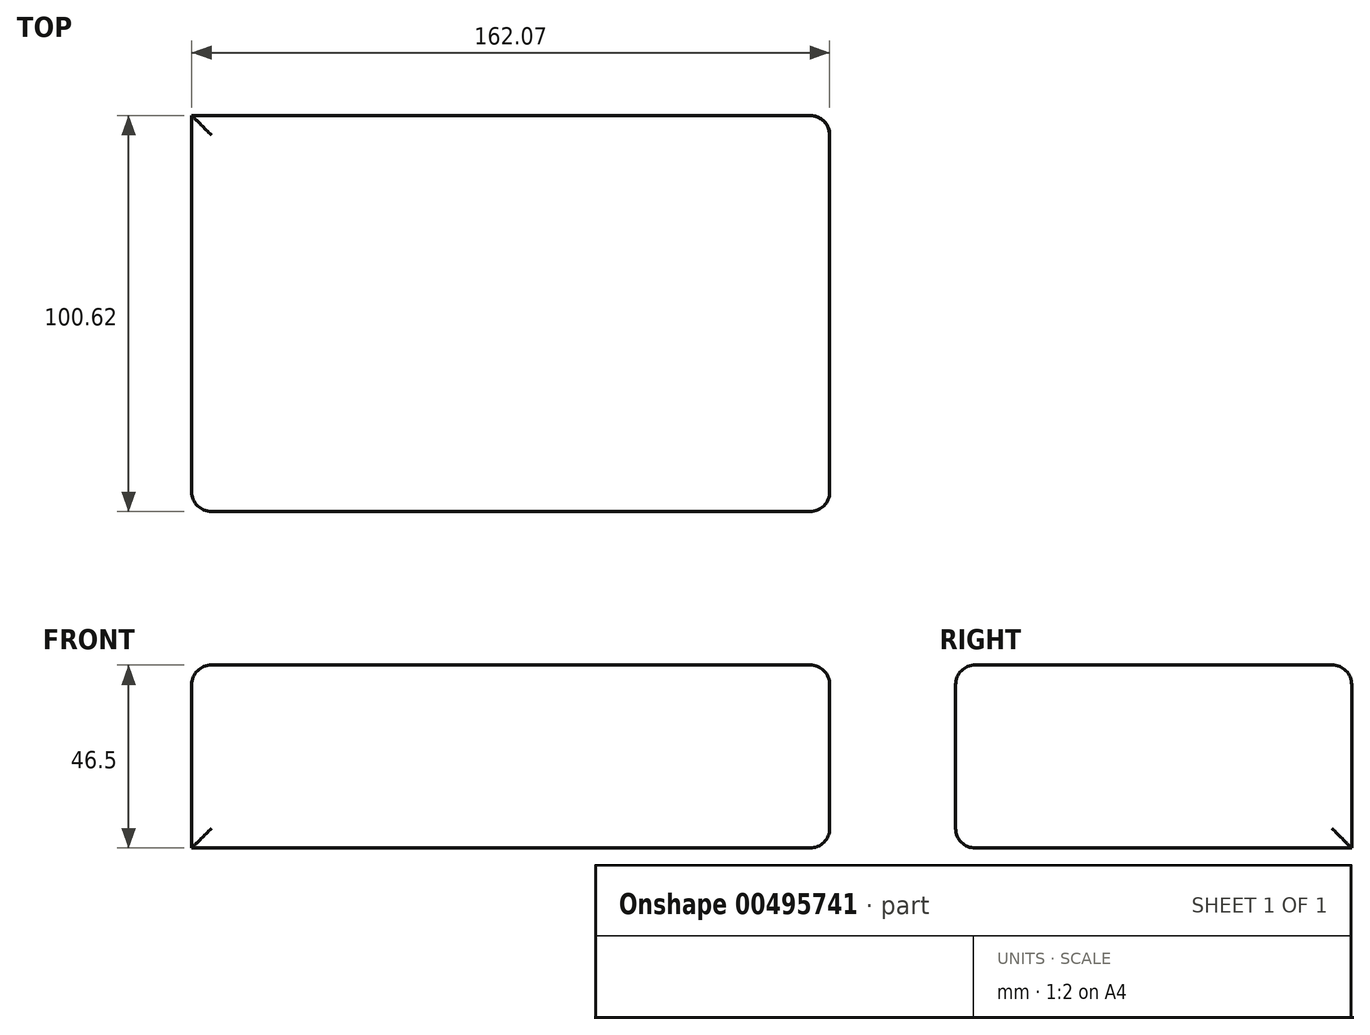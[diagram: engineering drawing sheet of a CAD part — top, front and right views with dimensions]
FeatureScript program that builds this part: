
annotation { "Feature Type Name" : "Feature", "Feature Type Description" : "" }
export const myFeature = defineFeature(function(context is Context, id is Id, definition is map)
    precondition{}
    {
        {
            var Q0;
            Q0=qCreatedBy(makeId("Top.planeOp"),FACE);
            var sketch = newSketch(context, id + "F0", { "sketchPlane" : qUnion([Q0])});
            skLineSegment(sketch, "E0.bottom", {"start": v(4.97, 0) * mm, "end": v(167.04, 0) * mm});
            skLineSegment(sketch, "E0.top", {"start": v(4.97, -100.62) * mm, "end": v(167.04, -100.62) * mm});
            skLineSegment(sketch, "E0.left", {"start": v(4.97, 0) * mm, "end": v(4.97, -100.62) * mm});
            skLineSegment(sketch, "E0.right", {"start": v(167.04, 0) * mm, "end": v(167.04, -100.62) * mm});
            skSolve(sketch);
        }
        {
            var Q0;
            Q0=makeQuery(id+"F0.imprint","IMPRINT",FACE,{"disambiguationData":[TD([[makeQuery(id+"F0.imprint","IMPRINT",EDGE,{"derivedFrom":sQuery(id+"F0.wireOp",EDGE,"E0.bottom")}),-1.0]])]});
            extrude(context, id + "F1", {"entities" : qUnion([Q0]), "depth" : 46.5 * mm});
        }
        {
            var Q0;
            Q0=makeQuery(id+"F1.opExtrude","CAP_EDGE",EDGE,{"disambiguationData":[OSD([sQuery(id+"F0.wireOp",EDGE,"E0.left")])],"isStart":false});
            var Q1;
            Q1=makeQuery(id+"F1.opExtrude","CAP_EDGE",EDGE,{"disambiguationData":[OSD([sQuery(id+"F0.wireOp",EDGE,"E0.top")])],"isStart":false});
            var Q2;
            Q2=makeQuery(id+"F1.opExtrude","CAP_EDGE",EDGE,{"disambiguationData":[OSD([sQuery(id+"F0.wireOp",EDGE,"E0.right")])],"isStart":false});
            var Q3;
            Q3=makeQuery(id+"F1.opExtrude","CAP_EDGE",EDGE,{"disambiguationData":[OSD([sQuery(id+"F0.wireOp",EDGE,"E0.bottom")])],"isStart":false});
            var Q4;
            Q4=makeQuery(id+"F1.opExtrude","CAP_EDGE",EDGE,{"disambiguationData":[OSD([sQuery(id+"F0.wireOp",EDGE,"E0.right")])],"isStart":true});
            var Q5;
            Q5=makeQuery(id+"F1.opExtrude","SWEPT_EDGE",EDGE,{"disambiguationData":[OSD([sQuery(id+"F0.wireOp",EDGE,"E0.top"),sQuery(id+"F0.wireOp",EDGE,"E0.right")])]});
            var Q6;
            Q6=makeQuery(id+"F1.opExtrude","SWEPT_EDGE",EDGE,{"disambiguationData":[OSD([sQuery(id+"F0.wireOp",EDGE,"E0.bottom"),sQuery(id+"F0.wireOp",EDGE,"E0.right")])]});
            var Q7;
            Q7=makeQuery(id+"F1.opExtrude","SWEPT_EDGE",EDGE,{"disambiguationData":[OSD([sQuery(id+"F0.wireOp",EDGE,"E0.top"),sQuery(id+"F0.wireOp",EDGE,"E0.left")])]});
            var Q8;
            Q8=makeQuery(id+"F1.opExtrude","CAP_EDGE",EDGE,{"disambiguationData":[OSD([sQuery(id+"F0.wireOp",EDGE,"E0.top")])],"isStart":true});
            fillet(context, id + "F2", {"entities" : qUnion([Q0, Q1, Q2, Q3, Q4, Q5, Q6, Q7, Q8]), "radius" : 5 * mm, "tangentPropagation" : true, "allowEdgeOverflow" : false});
        }
        {
            var Q0;
            Q0=makeQuery(id+"F1.opExtrude","CAP_FACE",FACE,{"disambiguationData":[OSD([sQuery(id+"F0.wireOp",EDGE,"E0.bottom"),sQuery(id+"F0.wireOp",EDGE,"E0.top"),sQuery(id+"F0.wireOp",EDGE,"E0.left"),sQuery(id+"F0.wireOp",EDGE,"E0.right")])],"isStart":false});
            var sketch = newSketch(context, id + "F3", { "sketchPlane" : qUnion([Q0])});
            skLineSegment(sketch, "E1.bottom", {"start": v(40.15, -67.74) * mm, "end": v(96.03, -67.74) * mm});
            skLineSegment(sketch, "E1.top", {"start": v(40.15, -79.2) * mm, "end": v(96.03, -79.2) * mm});
            skLineSegment(sketch, "E1.left", {"start": v(40.15, -67.74) * mm, "end": v(40.15, -79.2) * mm});
            skLineSegment(sketch, "E1.right", {"start": v(96.03, -67.74) * mm, "end": v(96.03, -79.2) * mm});
            skSolve(sketch);
        }
        {
            var Q0;
            Q0=makeQuery(id+"F3.imprint","IMPRINT",FACE,{"disambiguationData":[TD([[makeQuery(id+"F3.imprint","IMPRINT",EDGE,{"derivedFrom":sQuery(id+"F3.wireOp",EDGE,"E1.bottom")}),-1.0]])]});
            extrude(context, id + "F4", {"entities" : qUnion([Q0]), "operationType" : NewBodyOperationType.ADD, "oppositeDirection" : true, "depth" : 17.7 * mm});
        }
    });
